# Revit family: Reece_Bath_Base_Inset Bath_Sanitary Grade Acrylic_1520x715 mm
name_source: partatom
category: Plumbing Fixtures
revit_build: Autodesk Revit 2018 (Build: 20180329_1100(x64)
units: mm (PartAtom-declared; Revit-internal decimal feet)

## family parameters
Always vertical = Yes
Cut with Voids When Loaded = Yes
Part Type = Normal
Room Calculation Point = Yes
Round Connector Dimension = Use Diameter
Shared = Yes
Work Plane-Based = Yes

## types (1)
- 1520x715 mm_141 ltr_White
    Default Elevation = 0 mm  [stored 0 ft]
    Description = Inset Bath
    Disclaimer = THIS FILE IS THE PROPERTY OF THE REECE GROUP. IT MAY NOT BE REPRODUCED, REVERSE-ENGINEERED OR MODIFIED. ANY REPUBLICATION, TRANSMISSION OR DISTRIBUTION FOR THE PURPOSE OF COMMERCIALLY EXPLOITING THE FILES IS PROHIBITED.
    Keynote = Product #1792823, Reece_Bath_Base_Inset Bath_Sanitary Grade Acrylic_1520x715 mm - 1520x715 mm_141 ltr_White
    Manufacturer = Base
    Model = -
    Reece_Bath_Lip = 38 mm
    Reece_Bath_Outlet = 40 mm  [stored 0.131234 ft]
    Reece_Detail_Connector = Back Inlet
    Reece_Detail_Disclaimer = THIS FILE IS THE PROPERTY OF THE REECE GROUP. IT MAY NOT BE REPRODUCED, REVERSE-ENGINEERED OR MODIFIED. ANY REPUBLICATION, TRANSMISSION OR DISTRIBUTION FOR THE PURPOSE OF COMMERCIALLY EXPLOITING THE FILES IS PROHIBITED.
    Reece_Detail_Material = Sanitary Grade Acrylic
    Reece_Material_Main = Reece_Acrylic_White
    Reece_Material_Secondary = Reece_Brass_Chrome
    Reece_Overall_Capacity = 141 L
    Reece_Overall_Height = 380 mm
    Reece_Overall_Length = 1520 mm
    Reece_Overall_Width = 715 mm
    Reece_Product_Brand = Base
    Reece_Product_Description = Base Acrylic Bath 1520 x 715 x 380mm White
    Reece_Product_Mount = Inset
    Reece_Product_Number = 1792823
    Reece_Product_Sub Brand = -
    Reece_Product_Type = Bath
    Reece_Product_Web Page = https://www.reece.com.au
    Type Comments = Bath
    URL = https://www.reece.com.au

note: [stored X ft] marks values corroborated as IEEE doubles in the binary element streams (Revit-internal decimal feet)

## geometry (parser evidence)
native form markers: Sweep x3
no freeform markers — native parametric forms only
